# Revit family: Air_Gap-Zurn_Wilikns_Model_AG-13 - AG-14
name_source: partatom
category: Pipe Accessories
units: mm (PartAtom-declared; Revit-internal decimal feet)

## family parameters
Always vertical = Yes
Cut with Voids When Loaded = No
OmniClass Number = 23.65.55.14
OmniClass Title = Valves for Liquid Services
Part Type = Valve - Breaks Into
Round Connector Dimension = Use Radius
Shared = No
Work Plane-Based = No

## types (2) — shared parameters
Arm width = 0' - 1"
Assembly Code = D2020300
Base Height = 0' - 1 1/4"
Bolt Width = 0' - 0 3/16"
Bolt circle from End = 0' - 0 11/32"
Bolt hole Bush Dia = 0' - 0 5/8"
Bolt hole Dia = 0' - 0 1/4"
Bush Height = 0' - 0 1/8"
Default Elevation = 0' - 0"
Description = Air Gap Adaptor Fitting
Elbow Center = 1' - 3 1/16"
Flow Rate (GPM) = 0 GPM
Height = 1' - 0"
Length = 2' - 0"
Main Material = Paint - Zurn - Cast Grey Iron - Epoxy Blue
Manufacturer = Zurn Water, LLC
Manufacturer Brand = Zurn Wilkins
Max Working Water Pressure = 0.00 psi
Max Working Water Temperature = 0 °F
Modified Date = 07/02/2025
Product Documentation Link = https://files.zurn.com
Product Page URL = https://www.zurn.com
Product data URL = https://bimobject.com
Thickness = 0' - 0 1/4"
Top End Width = 0' - 2 1/8"
URL = www.zurn.com/

## per-type parameters (varying)
| type | BODY TOTAL LENGTH | Base Circle OD | Connector Center | Connector Plane | Connector Plane Center | Cut Height | DIM A DIA | DIM B LENGTH | DIM C INNER DIAMETER | Elbow | Elbow Top | MR Dia | Model | Nominal Diameter | Nominal Radius | OUTER RADIUS | PIPE Max Radius | Product Weight (lbs) | Top Cut Radius | Top Cut center | Top End Height | Top End Length |
| AG-13 (4" - 6" 475ST, 475STV Air Gap) | 0' - 10" | 0' - 4 1/4" | 0' - 8 23/32" | 0' - 10 21/32" | 0' - 8 23/32" | 0' - 6 1/4" | 0' - 5 3/8" | 1' - 2 1/2" | 0' - 3" | 4707A_Elbow : 4707- ELBOW | 1' - 1 1/4" | 0' - 5 5/8" | AG-13 | 0' - 3" | 0' - 1 1/2" | 0' - 2 1/8" | 0' - 2 11/16" | 9 | 0' - 1 19/32" | 0' - 1 5/16" | 0' - 0 13/16" | 0' - 3" |
| AG-14 (8"-10" 475ST, 475STV Air Gap) | 0' - 11" | 0' - 5 1/2" | 0' - 10 3/16" | 1' - 0 1/16" | 0' - 9 1/4" | 0' - 6 1/2" | 0' - 7" | 1' - 4 1/2" | 0' - 4" | 4711A_Elbow : 4711-ELBOW | 0' - 1 5/16" | 0' - 7 1/4" | AG-14 | 0' - 4" | 0' - 2" | 0' - 2 3/4" | 0' - 3 1/2" | 11 | 0' - 1 21/32" | 0' - 1 11/32" | 0' - 0 27/32" | 0' - 3 29/32" |

## geometry (parser evidence)
native form markers: Sweep x6
no freeform markers — native parametric forms only
